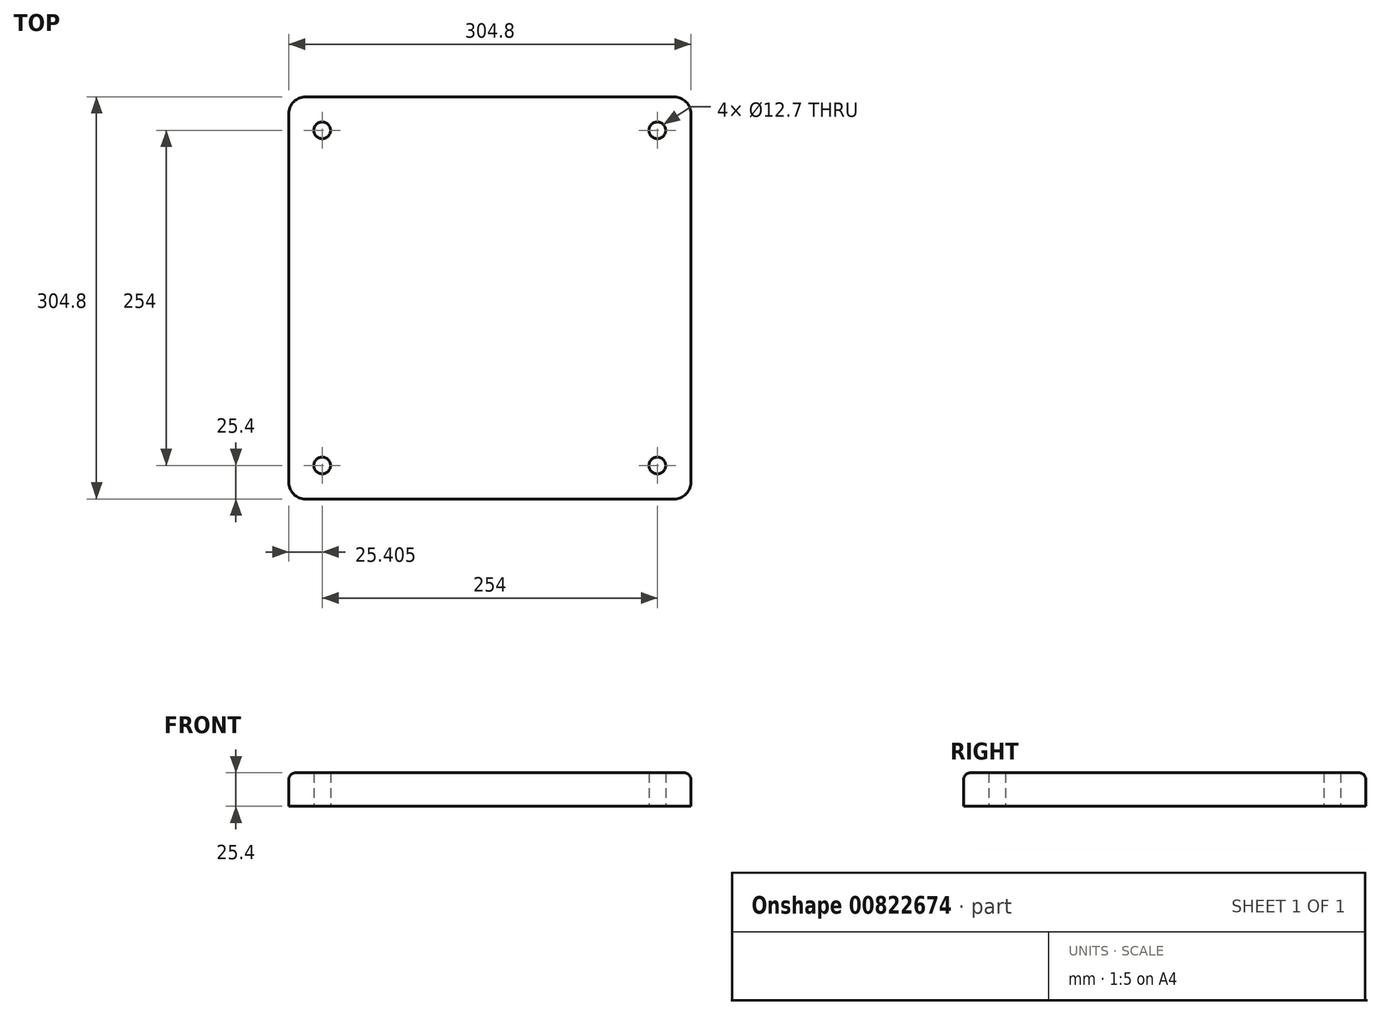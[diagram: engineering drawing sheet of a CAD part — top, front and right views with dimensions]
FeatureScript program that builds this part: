
annotation { "Feature Type Name" : "Feature", "Feature Type Description" : "" }
export const myFeature = defineFeature(function(context is Context, id is Id, definition is map)
    precondition{}
    {
        {
            var Q0;
            Q0=qCreatedBy(makeId("Top.planeOp"),FACE);
            var sketch = newSketch(context, id + "F0", { "sketchPlane" : qUnion([Q0])});
            skLineSegment(sketch, "E0.bottom", {"start": v(-121.37, 172.55) * mm, "end": v(158.03, 172.55) * mm});
            skLineSegment(sketch, "E0.top", {"start": v(-121.37, -132.25) * mm, "end": v(158.03, -132.25) * mm});
            skLineSegment(sketch, "E0.left", {"start": v(-134.07, 159.85) * mm, "end": v(-134.07, -119.55) * mm});
            skLineSegment(sketch, "E0.right", {"start": v(170.73, 159.85) * mm, "end": v(170.73, -119.55) * mm});
            skCircle(sketch, "E1", {"center": v(-108.67, 147.15) * mm, "radius": 6.35 * mm});
            skCircle(sketch, "E2", {"center": v(-108.67, -106.85) * mm, "radius": 6.35 * mm});
            skCircle(sketch, "E3", {"center": v(145.33, -106.85) * mm, "radius": 6.35 * mm});
            skCircle(sketch, "E4", {"center": v(145.33, 147.15) * mm, "radius": 6.35 * mm});
            skPoint(sketch, "E5.visualSharp", {"position": v(-134.07, 172.55) * mm});
            skArc(sketch, "E5.filletArc", {"start": v(-121.37, 172.55) * mm, "mid": v(-130.35, 168.83) * mm, "end": v(-134.07, 159.85) * mm});
            skPoint(sketch, "E6.visualSharp", {"position": v(-134.07, -132.25) * mm});
            skArc(sketch, "E6.filletArc", {"start": v(-134.07, -119.55) * mm, "mid": v(-130.35, -128.53) * mm, "end": v(-121.37, -132.25) * mm});
            skPoint(sketch, "E7.visualSharp", {"position": v(170.73, -132.25) * mm});
            skArc(sketch, "E7.filletArc", {"start": v(158.03, -132.25) * mm, "mid": v(167.02, -128.53) * mm, "end": v(170.73, -119.55) * mm});
            skPoint(sketch, "E8.visualSharp", {"position": v(170.73, 172.55) * mm});
            skArc(sketch, "E8.filletArc", {"start": v(170.73, 159.85) * mm, "mid": v(167.02, 168.83) * mm, "end": v(158.03, 172.55) * mm});
            skSolve(sketch);
        }
        {
            var Q0;
            Q0=makeQuery(id+"F0.imprint","IMPRINT",FACE,{"disambiguationData":[TD([[makeQuery(id+"F0.imprint","IMPRINT",EDGE,{"derivedFrom":sQuery(id+"F0.wireOp",EDGE,"E0.bottom")}),-1.0]])]});
            extrude(context, id + "F1", {"entities" : qUnion([Q0]), "depth" : 25.4 * mm, "offsetDistance" : 25.4 * mm});
        }
        {
            var Q0;
            Q0=makeQuery(id+"F1.opExtrude","CAP_EDGE",EDGE,{"disambiguationData":[OSD([sQuery(id+"F0.wireOp",EDGE,"E0.left")])],"isStart":false});
            var Q1;
            Q1=makeQuery(id+"F1.opExtrude","CAP_EDGE",EDGE,{"disambiguationData":[OSD([sQuery(id+"F0.wireOp",EDGE,"E6.filletArc")])],"isStart":false});
            var Q2;
            Q2=makeQuery(id+"F1.opExtrude","CAP_EDGE",EDGE,{"disambiguationData":[OSD([sQuery(id+"F0.wireOp",EDGE,"E0.top")])],"isStart":false});
            var Q3;
            Q3=makeQuery(id+"F1.opExtrude","CAP_EDGE",EDGE,{"disambiguationData":[OSD([sQuery(id+"F0.wireOp",EDGE,"E7.filletArc")])],"isStart":false});
            var Q4;
            Q4=makeQuery(id+"F1.opExtrude","CAP_EDGE",EDGE,{"disambiguationData":[OSD([sQuery(id+"F0.wireOp",EDGE,"E0.right")])],"isStart":false});
            var Q5;
            Q5=makeQuery(id+"F1.opExtrude","CAP_EDGE",EDGE,{"disambiguationData":[OSD([sQuery(id+"F0.wireOp",EDGE,"E8.filletArc")])],"isStart":false});
            var Q6;
            Q6=makeQuery(id+"F1.opExtrude","CAP_EDGE",EDGE,{"disambiguationData":[OSD([sQuery(id+"F0.wireOp",EDGE,"E0.bottom")])],"isStart":false});
            var Q7;
            Q7=makeQuery(id+"F1.opExtrude","CAP_EDGE",EDGE,{"disambiguationData":[OSD([sQuery(id+"F0.wireOp",EDGE,"E5.filletArc")])],"isStart":false});
            fillet(context, id + "F2", {"entities" : qUnion([Q0, Q1, Q2, Q3, Q4, Q5, Q6, Q7]), "radius" : 5.08 * mm, "tangentPropagation" : true, "allowEdgeOverflow" : false});
        }
    });
